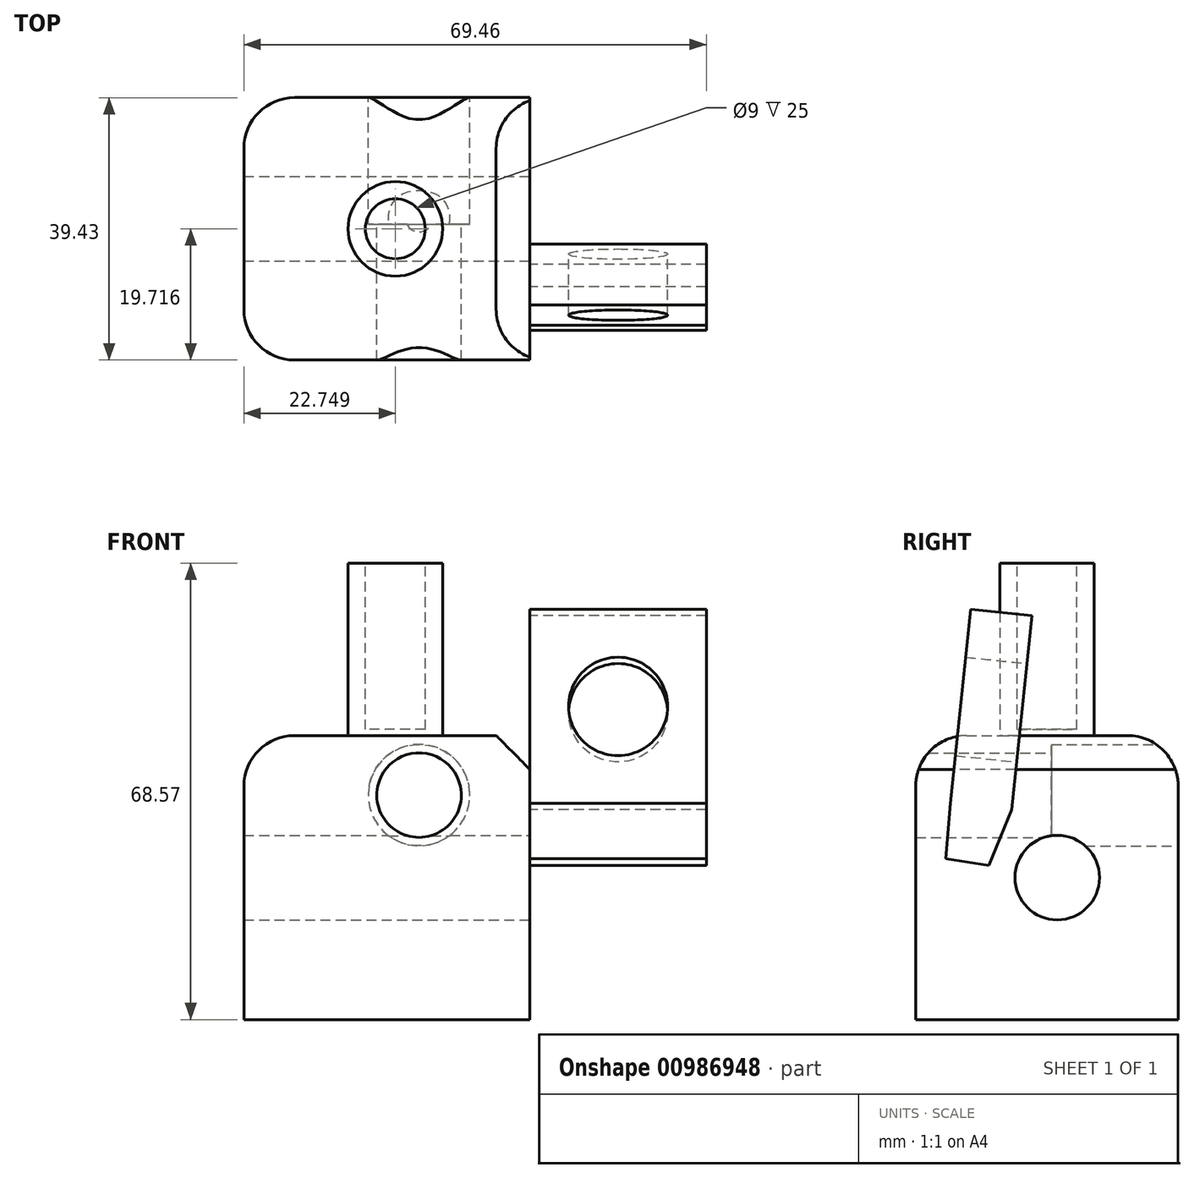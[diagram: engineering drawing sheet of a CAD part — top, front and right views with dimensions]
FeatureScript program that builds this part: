
annotation { "Feature Type Name" : "Feature", "Feature Type Description" : "" }
export const myFeature = defineFeature(function(context is Context, id is Id, definition is map)
    precondition{}
    {
        {
            var Q0;
            Q0=qCreatedBy(makeId("Top.planeOp"),FACE);
            var sketch = newSketch(context, id + "F0", { "sketchPlane" : qUnion([Q0])});
            skLineSegment(sketch, "E0.bottom", {"start": v(-18.67, -21.25) * mm, "end": v(24.29, -21.25) * mm});
            skLineSegment(sketch, "E0.top", {"start": v(-18.67, 18.18) * mm, "end": v(24.29, 18.18) * mm});
            skLineSegment(sketch, "E0.left", {"start": v(-18.67, -21.25) * mm, "end": v(-18.67, 18.18) * mm});
            skLineSegment(sketch, "E0.right", {"start": v(24.29, -21.25) * mm, "end": v(24.29, 18.18) * mm});
            skSolve(sketch);
        }
        {
            var Q0;
            Q0=makeQuery(id+"F0.imprint","IMPRINT",FACE,{"disambiguationData":[TD([[makeQuery(id+"F0.imprint","IMPRINT",EDGE,{"derivedFrom":sQuery(id+"F0.wireOp",EDGE,"E0.bottom")}),1.0]])]});
            extrude(context, id + "F1", {"entities" : qUnion([Q0]), "depth" : 42.67 * mm, "offsetDistance" : 25.4 * mm});
        }
        {
            var Q0;
            Q0=makeQuery(id+"F1.opExtrude","SWEPT_FACE",FACE,{"disambiguationData":[OSD([sQuery(id+"F0.wireOp",EDGE,"E0.right")])]});
            var sketch = newSketch(context, id + "F2", { "sketchPlane" : qUnion([Q0])});
            skPoint(sketch, "E1", {"position": v(0, 21.34) * mm});
            skPoint(sketch, "E1.positionSnap0", {"position": v(-21.25, 21.34) * mm});
            skSolve(sketch);
        }
        {
            var Q0;
            Q0=sQuery(id+"F2.wireOp",VERTEX,"E1");
            var Q1;
            Q1=makeQuery(id+"F1.opExtrude","SWEPT_BODY",BODY,{"disambiguationData":[OSD([sQuery(id+"F0.wireOp",EDGE,"E0.bottom"),sQuery(id+"F0.wireOp",EDGE,"E0.top"),sQuery(id+"F0.wireOp",EDGE,"E0.left"),sQuery(id+"F0.wireOp",EDGE,"E0.right")])]});
            hole(context, id + "F3", {"style" : HoleStyle.SIMPLE, "endStyle" : HoleEndStyle.BLIND, "holeDiameter" : 12.7 * mm, "majorDiameter" : 6.35 * mm, "holeDepth" : 50.8 * mm, "isTappedThrough" : true, "tappedDepth" : 12.7 * mm, "tapClearance" : 3, "locations" : qUnion([Q0]), "scope" : qUnion([Q1])});
        }
        {
            var Q0;
            Q0=makeQuery(id+"F1.opExtrude","SWEPT_FACE",FACE,{"disambiguationData":[OSD([sQuery(id+"F0.wireOp",EDGE,"E0.top")])]});
            var sketch = newSketch(context, id + "F4", { "sketchPlane" : qUnion([Q0])});
            skLineSegment(sketch, "E2", {"start": v(-24.29, 42.67) * mm, "end": v(-7.64, 42.67) * mm});
            skLineSegment(sketch, "E3", {"start": v(-7.64, 42.67) * mm, "end": v(-7.64, 33.72) * mm});
            skSolve(sketch);
        }
        {
            var Q0;
            Q0=sQuery(id+"F4.wireOp",VERTEX,"E3.end");
            var Q1;
            Q1=makeQuery(id+"F1.opExtrude","SWEPT_BODY",BODY,{"disambiguationData":[OSD([sQuery(id+"F0.wireOp",EDGE,"E0.bottom"),sQuery(id+"F0.wireOp",EDGE,"E0.top"),sQuery(id+"F0.wireOp",EDGE,"E0.left"),sQuery(id+"F0.wireOp",EDGE,"E0.right")])]});
            hole(context, id + "F5", {"style" : HoleStyle.C_BORE, "endStyle" : HoleEndStyle.THROUGH, "holeDiameter" : 12.7 * mm, "cBoreDiameter" : 15.24 * mm, "cBoreDepth" : 19.05 * mm, "majorDiameter" : 6.35 * mm, "isTappedThrough" : true, "tappedDepth" : 12.7 * mm, "tapClearance" : 3, "locations" : qUnion([Q0]), "scope" : qUnion([Q1])});
        }
        {
            var Q0;
            Q0=makeQuery(id+"F1.opExtrude","CAP_EDGE",EDGE,{"disambiguationData":[OSD([sQuery(id+"F0.wireOp",EDGE,"E0.right")])],"isStart":false});
            chamfer(context, id + "F6", {"entities" : qUnion([Q0]), "width" : 5.08 * mm, "tangentPropagation" : true});
        }
        {
            var Q0;
            Q0=makeQuery(id+"F1.opExtrude","SWEPT_EDGE",EDGE,{"disambiguationData":[OSD([sQuery(id+"F0.wireOp",EDGE,"E0.top"),sQuery(id+"F0.wireOp",EDGE,"E0.left")])]});
            var Q1;
            Q1=makeQuery(id+"F1.opExtrude","CAP_EDGE",EDGE,{"disambiguationData":[OSD([sQuery(id+"F0.wireOp",EDGE,"E0.top")])],"isStart":false});
            var Q2;
            Q2=makeQuery(id+"F1.opExtrude","CAP_EDGE",EDGE,{"disambiguationData":[OSD([sQuery(id+"F0.wireOp",EDGE,"E0.left")])],"isStart":false});
            var Q3;
            Q3=makeQuery(id+"F1.opExtrude","SWEPT_EDGE",EDGE,{"disambiguationData":[OSD([sQuery(id+"F0.wireOp",EDGE,"E0.bottom"),sQuery(id+"F0.wireOp",EDGE,"E0.left")])]});
            var Q4;
            Q4=makeQuery(id+"F1.opExtrude","CAP_EDGE",EDGE,{"disambiguationData":[OSD([sQuery(id+"F0.wireOp",EDGE,"E0.bottom")])],"isStart":false});
            fillet(context, id + "F7", {"entities" : qUnion([Q0, Q1, Q2, Q3, Q4]), "radius" : 7.62 * mm, "tangentPropagation" : true, "allowEdgeOverflow" : false});
        }
        {
            var Q0;
            Q0=makeQuery(id+"F1.opExtrude","SWEPT_FACE",FACE,{"disambiguationData":[OSD([sQuery(id+"F0.wireOp",EDGE,"E0.right")])]});
            var sketch = newSketch(context, id + "F8", { "sketchPlane" : qUnion([Q0])});
            skLineSegment(sketch, "E4", {"start": v(18.18, 0) * mm, "end": v(3.73, 16.2) * mm});
            skPoint(sketch, "E5", {"position": v(10.96, 8.1) * mm});
            skPoint(sketch, "E6", {"position": v(5.75, 13.94) * mm});
            skSolve(sketch);
        }
        {
            var Q0;
            {var subQ0=sQuery(id+"F0.wireOp",EDGE,"E0.right");Q0=makeQuery(id+"F8.imprint","IMPRINT",FACE,{"disambiguationData":[TD([[makeQuery(id+"F8.imprint","IMPRINT",EDGE,{"derivedFrom":makeQuery(id+"F1.opExtrude","CAP_EDGE",EDGE,{"disambiguationData":[OSD([subQ0])],"isStart":true})}),1.0]])]});}
            var sketch = newSketch(context, id + "F9", { "sketchPlane" : qUnion([Q0])});
            skCircle(sketch, "E7", {"center": v(11.04, 8.32) * mm, "radius": 5.56 * mm});
            skSolve(sketch);
        }
        {
            var Q0;
            Q0=sQuery(id+"F9.wireOp",EDGE,"E7");
            extrude(context, id + "F10", {"bodyType" : ToolBodyType.SURFACE, "surfaceEntities" : qUnion([Q0]), "depth" : 20.2 * mm, "offsetDistance" : 25 * mm});
        }
        {
            var Q0;
            Q0=makeQuery(id+"F1.opExtrude","CAP_FACE",FACE,{"disambiguationData":[OSD([sQuery(id+"F0.wireOp",EDGE,"E0.bottom"),sQuery(id+"F0.wireOp",EDGE,"E0.top"),sQuery(id+"F0.wireOp",EDGE,"E0.left"),sQuery(id+"F0.wireOp",EDGE,"E0.right")])],"isStart":false});
            var sketch = newSketch(context, id + "F11", { "sketchPlane" : qUnion([Q0])});
            skPoint(sketch, "E8", {"position": v(4.08, -1.53) * mm});
            skCircle(sketch, "E9", {"center": v(4.08, -1.53) * mm, "radius": 7.1 * mm});
            skSolve(sketch);
        }
        {
            var Q0;
            Q0=makeQuery(id+"F11.imprint","IMPRINT",FACE,{"disambiguationData":[TD([[makeQuery(id+"F11.imprint","IMPRINT",EDGE,{"derivedFrom":sQuery(id+"F11.wireOp",EDGE,"E9")}),1.0]])]});
            extrude(context, id + "F12", {"entities" : qUnion([Q0]), "operationType" : NewBodyOperationType.ADD, "depth" : 25.9 * mm, "offsetDistance" : 25 * mm});
        }
        {
            var Q0;
            {var subQ0=sQuery(id+"F0.wireOp",EDGE,"E0.right");Q0=makeQuery(id+"F8.imprint","IMPRINT",FACE,{"disambiguationData":[TD([[makeQuery(id+"F8.imprint","IMPRINT",EDGE,{"derivedFrom":makeQuery(id+"F1.opExtrude","CAP_EDGE",EDGE,{"disambiguationData":[OSD([subQ0])],"isStart":true})}),1.0]])]});}
            var sketch = newSketch(context, id + "F13", { "sketchPlane" : qUnion([Q0])});
            skLineSegment(sketch, "E10", {"start": v(-16.04, 32.48) * mm, "end": v(-6.86, 31.51) * mm});
            skLineSegment(sketch, "E11", {"start": v(-6.86, 31.51) * mm, "end": v(-10.24, 23.18) * mm});
            skLineSegment(sketch, "E12", {"start": v(-10.24, 23.18) * mm, "end": v(-16.76, 24.15) * mm});
            skLineSegment(sketch, "E13", {"start": v(-16.76, 24.15) * mm, "end": v(-16.04, 32.48) * mm});
            skSolve(sketch);
        }
        {
            var Q0;
            Q0=makeQuery(id+"F13.imprint","IMPRINT",FACE,{"disambiguationData":[TD([[makeQuery(id+"F13.imprint","IMPRINT",EDGE,{"derivedFrom":sQuery(id+"F13.wireOp",EDGE,"E10")}),-1.0]])]});
            extrude(context, id + "F14", {"entities" : qUnion([Q0]), "operationType" : NewBodyOperationType.ADD, "depth" : 26.5 * mm, "offsetDistance" : 25 * mm});
        }
        {
            var Q0;
            Q0=makeQuery(id+"F14.opExtrude","SWEPT_FACE",FACE,{"disambiguationData":[OSD([sQuery(id+"F13.wireOp",EDGE,"E10")])]});
            extrude(context, id + "F15", {"entities" : qUnion([Q0]), "operationType" : NewBodyOperationType.ADD, "depth" : 29.3 * mm, "offsetDistance" : 25 * mm});
        }
        {
            var Q0;
            Q0=makeQuery(id+"F12.opExtrude","CAP_FACE",FACE,{"disambiguationData":[OSD([sQuery(id+"F11.wireOp",EDGE,"E9")])],"isStart":false});
            var sketch = newSketch(context, id + "F16", { "sketchPlane" : qUnion([Q0])});
            skCircle(sketch, "E14", {"center": v(4.08, -1.53) * mm, "radius": 4.5 * mm});
            skSolve(sketch);
        }
        {
            var Q0;
            Q0=makeQuery(id+"F16.imprint","IMPRINT",FACE,{"disambiguationData":[TD([[makeQuery(id+"F16.imprint","IMPRINT",EDGE,{"derivedFrom":sQuery(id+"F16.wireOp",EDGE,"E14")}),1.0]])]});
            extrude(context, id + "F17", {"entities" : qUnion([Q0]), "operationType" : NewBodyOperationType.REMOVE, "oppositeDirection" : true, "depth" : 25 * mm, "offsetDistance" : 25 * mm});
        }
        {
            var Q0;
            Q0=makeQuery(id+"F15.opExtrude","SWEPT_FACE",FACE,{"disambiguationData":[OSD([sQuery(id+"F13.wireOp",EDGE,"E10"),sQuery(id+"F13.wireOp",EDGE,"E11")])]});
            var sketch = newSketch(context, id + "F18", { "sketchPlane" : qUnion([Q0])});
            skCircle(sketch, "E15", {"center": v(-37.54, 45.27) * mm, "radius": 7.44 * mm});
            skSolve(sketch);
        }
        {
            var Q0;
            Q0=makeQuery(id+"F18.imprint","IMPRINT",FACE,{"disambiguationData":[TD([[makeQuery(id+"F18.imprint","IMPRINT",EDGE,{"derivedFrom":sQuery(id+"F18.wireOp",EDGE,"E15")}),1.0]])]});
            extrude(context, id + "F19", {"entities" : qUnion([Q0]), "operationType" : NewBodyOperationType.REMOVE, "oppositeDirection" : true, "depth" : 25 * mm, "offsetDistance" : 25 * mm});
        }
    });
